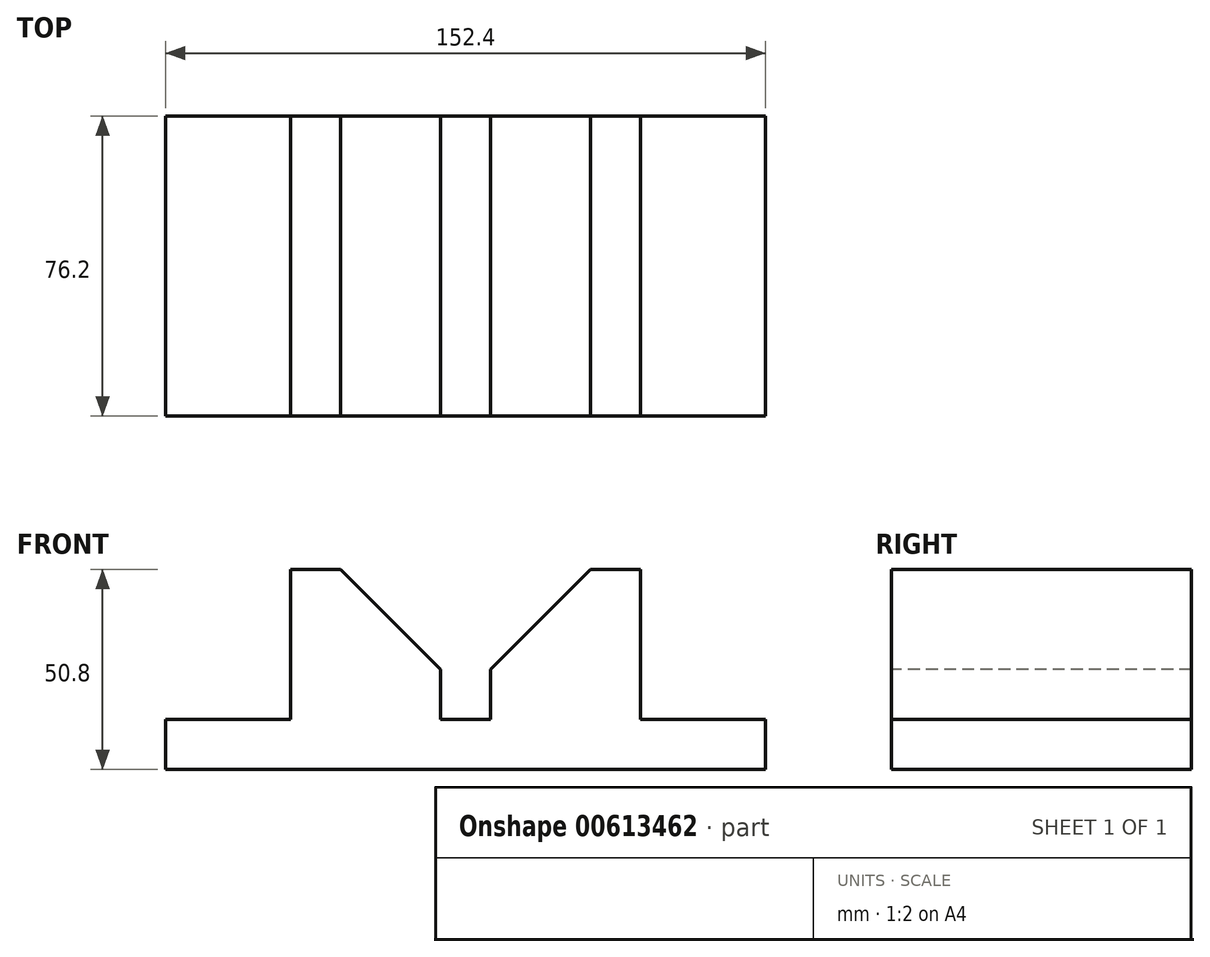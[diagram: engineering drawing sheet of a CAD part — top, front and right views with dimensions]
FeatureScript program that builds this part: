
annotation { "Feature Type Name" : "Feature", "Feature Type Description" : "" }
export const myFeature = defineFeature(function(context is Context, id is Id, definition is map)
    precondition{}
    {
        {
            var Q0;
            Q0=qCreatedBy(makeId("Front.planeOp"),FACE);
            var sketch = newSketch(context, id + "F0", { "sketchPlane" : qUnion([Q0])});
            skLineSegment(sketch, "E0", {"start": v(0, 0) * mm, "end": v(0, 12.7) * mm});
            skLineSegment(sketch, "E1", {"start": v(0, 12.7) * mm, "end": v(31.75, 12.7) * mm});
            skLineSegment(sketch, "E2", {"start": v(31.75, 12.7) * mm, "end": v(31.75, 50.8) * mm});
            skLineSegment(sketch, "E3", {"start": v(31.75, 50.8) * mm, "end": v(69.85, 50.8) * mm});
            skLineSegment(sketch, "E4", {"start": v(69.85, 50.8) * mm, "end": v(69.85, 12.7) * mm});
            skLineSegment(sketch, "E5", {"start": v(69.85, 12.7) * mm, "end": v(82.55, 12.7) * mm});
            skLineSegment(sketch, "E6", {"start": v(82.55, 12.7) * mm, "end": v(82.55, 50.8) * mm});
            skLineSegment(sketch, "E7", {"start": v(82.55, 50.8) * mm, "end": v(120.65, 50.8) * mm});
            skLineSegment(sketch, "E8", {"start": v(120.65, 50.8) * mm, "end": v(120.65, 12.7) * mm});
            skLineSegment(sketch, "E9", {"start": v(120.65, 12.7) * mm, "end": v(152.4, 12.7) * mm});
            skLineSegment(sketch, "E10", {"start": v(152.4, 12.7) * mm, "end": v(152.4, 0) * mm});
            skLineSegment(sketch, "E11", {"start": v(152.4, 0) * mm, "end": v(0, 0) * mm});
            skSolve(sketch);
        }
        {
            var Q0;
            Q0=makeQuery(id+"F0.imprint","IMPRINT",FACE,{"disambiguationData":[TD([[makeQuery(id+"F0.imprint","IMPRINT",EDGE,{"derivedFrom":sQuery(id+"F0.wireOp",EDGE,"E0")}),-1.0]])]});
            extrude(context, id + "F1", {"entities" : qUnion([Q0]), "oppositeDirection" : true, "depth" : 76.2 * mm, "offsetDistance" : 25.4 * mm});
        }
        {
            var Q0;
            Q0=makeQuery(id+"F1.opExtrude","CAP_FACE",FACE,{"disambiguationData":[OSD([sQuery(id+"F0.wireOp",EDGE,"E0"),sQuery(id+"F0.wireOp",EDGE,"E1"),sQuery(id+"F0.wireOp",EDGE,"E2"),sQuery(id+"F0.wireOp",EDGE,"E3"),sQuery(id+"F0.wireOp",EDGE,"E4"),sQuery(id+"F0.wireOp",EDGE,"E5"),sQuery(id+"F0.wireOp",EDGE,"E6"),sQuery(id+"F0.wireOp",EDGE,"E7"),sQuery(id+"F0.wireOp",EDGE,"E8"),sQuery(id+"F0.wireOp",EDGE,"E9"),sQuery(id+"F0.wireOp",EDGE,"E10"),sQuery(id+"F0.wireOp",EDGE,"E11")])],"isStart":true});
            var sketch = newSketch(context, id + "F2", { "sketchPlane" : qUnion([Q0])});
            skLineSegment(sketch, "E12", {"start": v(44.45, 50.8) * mm, "end": v(69.85, 25.4) * mm});
            skLineSegment(sketch, "E13", {"start": v(69.85, 25.4) * mm, "end": v(69.85, 50.8) * mm});
            skLineSegment(sketch, "E14", {"start": v(69.85, 50.8) * mm, "end": v(44.45, 50.8) * mm});
            skSolve(sketch);
        }
        {
            var Q0;
            Q0=makeQuery(id+"F2.imprint","IMPRINT",FACE,{"disambiguationData":[TD([[makeQuery(id+"F2.imprint","IMPRINT",EDGE,{"derivedFrom":sQuery(id+"F2.wireOp",EDGE,"E12")}),1.0]])]});
            extrude(context, id + "F3", {"entities" : qUnion([Q0]), "operationType" : NewBodyOperationType.REMOVE, "oppositeDirection" : true, "depth" : 76.2 * mm, "offsetDistance" : 25.4 * mm});
        }
        {
            var Q0;
            Q0=makeQuery(id+"F1.opExtrude","CAP_FACE",FACE,{"disambiguationData":[OSD([sQuery(id+"F0.wireOp",EDGE,"E0"),sQuery(id+"F0.wireOp",EDGE,"E1"),sQuery(id+"F0.wireOp",EDGE,"E2"),sQuery(id+"F0.wireOp",EDGE,"E3"),sQuery(id+"F0.wireOp",EDGE,"E4"),sQuery(id+"F0.wireOp",EDGE,"E5"),sQuery(id+"F0.wireOp",EDGE,"E6"),sQuery(id+"F0.wireOp",EDGE,"E7"),sQuery(id+"F0.wireOp",EDGE,"E8"),sQuery(id+"F0.wireOp",EDGE,"E9"),sQuery(id+"F0.wireOp",EDGE,"E10"),sQuery(id+"F0.wireOp",EDGE,"E11")])],"isStart":true});
            var sketch = newSketch(context, id + "F4", { "sketchPlane" : qUnion([Q0])});
            skLineSegment(sketch, "E15", {"start": v(82.55, 25.4) * mm, "end": v(107.95, 50.8) * mm});
            skLineSegment(sketch, "E16", {"start": v(107.95, 50.8) * mm, "end": v(82.55, 50.8) * mm});
            skLineSegment(sketch, "E17", {"start": v(82.55, 50.8) * mm, "end": v(82.55, 25.4) * mm});
            skSolve(sketch);
        }
        {
            var Q0;
            Q0=makeQuery(id+"F4.imprint","IMPRINT",FACE,{"disambiguationData":[TD([[makeQuery(id+"F4.imprint","IMPRINT",EDGE,{"derivedFrom":sQuery(id+"F4.wireOp",EDGE,"E15")}),1.0]])]});
            extrude(context, id + "F5", {"entities" : qUnion([Q0]), "operationType" : NewBodyOperationType.REMOVE, "oppositeDirection" : true, "depth" : 76.2 * mm, "offsetDistance" : 25.4 * mm});
        }
    });
